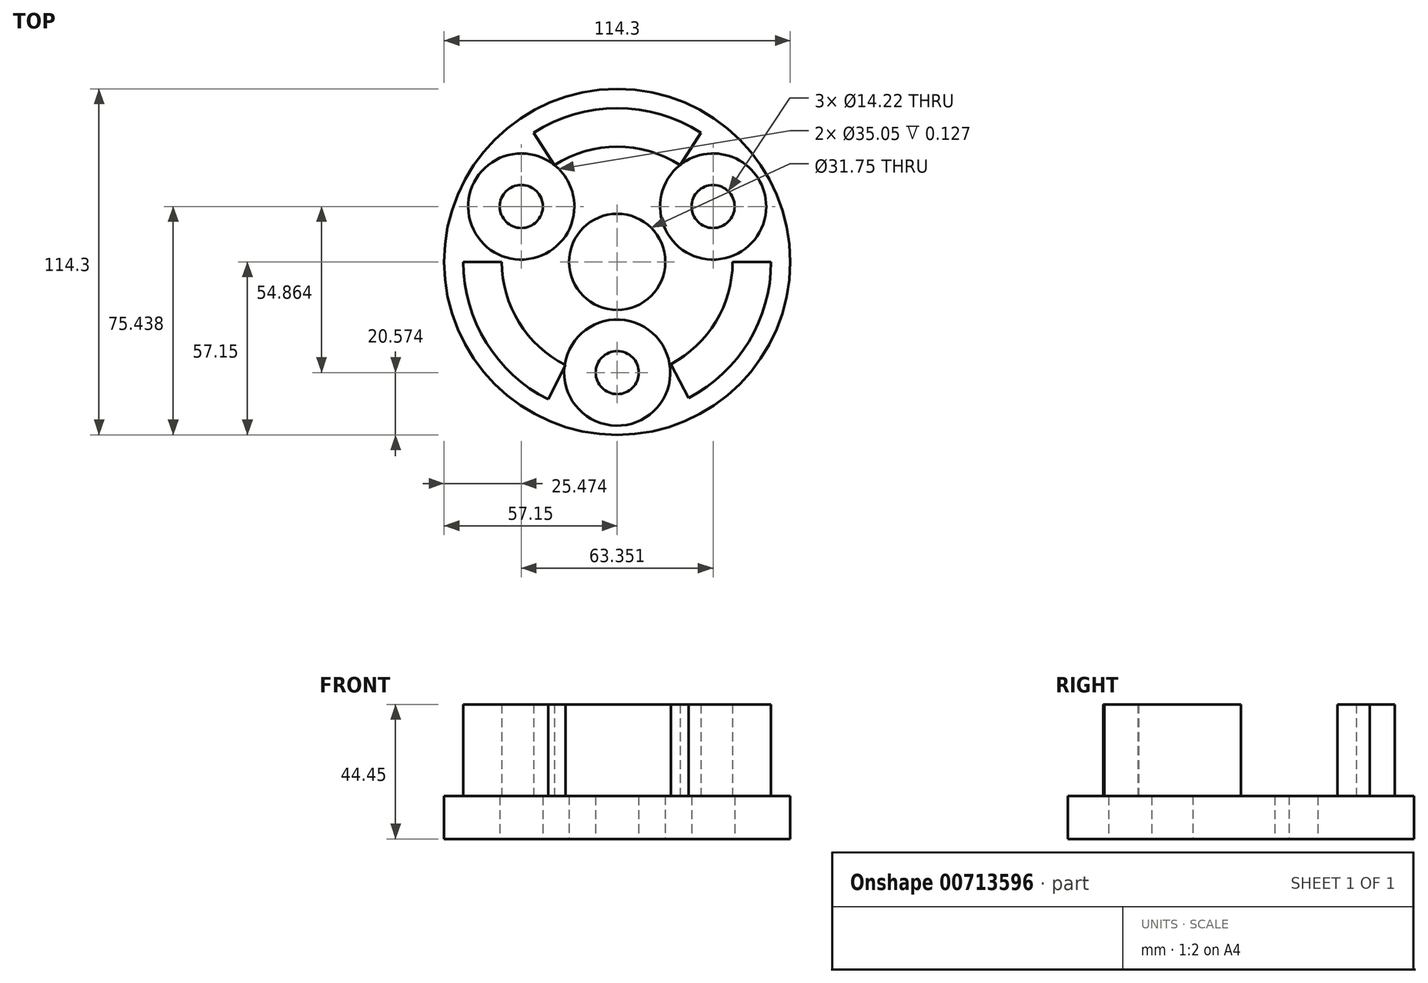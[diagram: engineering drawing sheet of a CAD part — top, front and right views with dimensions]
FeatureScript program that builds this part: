
annotation { "Feature Type Name" : "Feature", "Feature Type Description" : "" }
export const myFeature = defineFeature(function(context is Context, id is Id, definition is map)
    precondition{}
    {
        {
            var Q0;
            Q0=qCreatedBy(makeId("Top.planeOp"),FACE);
            var sketch = newSketch(context, id + "F0", { "sketchPlane" : qUnion([Q0])});
            skCircle(sketch, "E0", {"center": v(0, 0) * mm, "radius": 57.15 * mm});
            skCircle(sketch, "E1", {"center": v(0, 0) * mm, "radius": 36.58 * mm, "construction": true});
            skCircle(sketch, "E2", {"center": v(0, -36.58) * mm, "radius": 7.11 * mm});
            skCircle(sketch, "E3.1.0", {"center": v(31.68, 18.29) * mm, "radius": 7.11 * mm});
            skCircle(sketch, "E3.2.0", {"center": v(-31.68, 18.29) * mm, "radius": 7.11 * mm});
            skLineSegment(sketch, "E4", {"start": v(0, 0) * mm, "end": v(-31.68, 18.29) * mm});
            skLineSegment(sketch, "E5", {"start": v(0, 0) * mm, "end": v(31.68, 18.29) * mm});
            skLineSegment(sketch, "E6", {"start": v(0, 0) * mm, "end": v(0, -36.58) * mm});
            skCircle(sketch, "E7", {"center": v(0, 0) * mm, "radius": 15.88 * mm});
            skSolve(sketch);
        }
        {
            var Q0;
            Q0 = qSketchRegion(id + "F0", true);
            extrude(context, id + "F1", {"entities" : qUnion([Q0]), "depth" : 14.22 * mm, "offsetDistance" : 25.4 * mm});
        }
        {
            var Q0;
            Q0=makeQuery(id+"F1.opExtrude","CAP_FACE",FACE,{"disambiguationData":[OSD([sQuery(id+"F0.wireOp",EDGE,"E0"),sQuery(id+"F0.wireOp",EDGE,"E2"),sQuery(id+"F0.wireOp",EDGE,"E3.1.0"),sQuery(id+"F0.wireOp",EDGE,"E3.2.0")])],"isStart":false});
            var sketch = newSketch(context, id + "F2", { "sketchPlane" : qUnion([Q0])});
            skArc(sketch, "E8", {"start": v(-38.1, 0) * mm, "mid": v(-32.43, -20) * mm, "end": v(-17.12, -34.04) * mm});
            skArc(sketch, "E9.0", {"start": v(-50.8, 0) * mm, "mid": v(-43.24, -26.66) * mm, "end": v(-22.83, -45.38) * mm});
            skArc(sketch, "E10.trimOffspring", {"start": v(20.72, 31.97) * mm, "mid": v(0, 38.1) * mm, "end": v(-20.72, 31.97) * mm});
            skArc(sketch, "E11.trimOffspring", {"start": v(17.69, -33.74) * mm, "mid": v(32.6, -19.72) * mm, "end": v(38.1, 0) * mm});
            skLineSegment(sketch, "E12", {"start": v(-20.72, 31.97) * mm, "end": v(-27.63, 42.63) * mm});
            skLineSegment(sketch, "E13", {"start": v(20.72, 31.97) * mm, "end": v(27.63, 42.63) * mm});
            skArc(sketch, "E14.trimOffspring", {"start": v(27.63, 42.63) * mm, "mid": v(0, 50.8) * mm, "end": v(-27.63, 42.63) * mm});
            skLineSegment(sketch, "E15", {"start": v(-38.1, 0) * mm, "end": v(-50.8, 0) * mm});
            skLineSegment(sketch, "E16", {"start": v(-17.12, -34.04) * mm, "end": v(-22.83, -45.38) * mm});
            skLineSegment(sketch, "E17", {"start": v(17.69, -33.74) * mm, "end": v(23.59, -45) * mm});
            skLineSegment(sketch, "E18", {"start": v(38.1, 0) * mm, "end": v(50.8, 0) * mm});
            skArc(sketch, "E19.trimOffspring", {"start": v(23.59, -45) * mm, "mid": v(43.47, -26.3) * mm, "end": v(50.8, 0) * mm});
            skSolve(sketch);
        }
        {
            var Q0;
            Q0 = qSketchRegion(id + "F2", true);
            extrude(context, id + "F3", {"entities" : qUnion([Q0]), "operationType" : NewBodyOperationType.ADD, "depth" : 30.23 * mm, "offsetDistance" : 25.4 * mm});
        }
        {
            var Q0;
            Q0=makeQuery(id+"F1.opExtrude","CAP_FACE",FACE,{"disambiguationData":[OSD([sQuery(id+"F0.wireOp",EDGE,"E0"),sQuery(id+"F0.wireOp",EDGE,"E2"),sQuery(id+"F0.wireOp",EDGE,"E3.1.0"),sQuery(id+"F0.wireOp",EDGE,"E3.2.0"),sQuery(id+"F0.wireOp",EDGE,"E7")])],"isStart":false});
            var sketch = newSketch(context, id + "F4", { "sketchPlane" : qUnion([Q0])});
            skCircle(sketch, "E20", {"center": v(-31.68, 18.29) * mm, "radius": 17.53 * mm});
            skCircle(sketch, "E21", {"center": v(31.68, 18.29) * mm, "radius": 17.53 * mm});
            skCircle(sketch, "E22", {"center": v(0, -36.58) * mm, "radius": 17.53 * mm});
            skSolve(sketch);
        }
        {
            var Q0;
            Q0=makeQuery(id+"F4.imprint","IMPRINT",FACE,{"disambiguationData":[TD([[makeQuery(id+"F4.imprint","IMPRINT",EDGE,{"derivedFrom":sQuery(id+"F4.wireOp",EDGE,"E20")}),1.0]])]});
            var Q1;
            Q1=makeQuery(id+"F4.imprint","IMPRINT",FACE,{"disambiguationData":[TD([[makeQuery(id+"F4.imprint","IMPRINT",EDGE,{"derivedFrom":sQuery(id+"F4.wireOp",EDGE,"E21")}),1.0]])]});
            var Q2;
            Q2=makeQuery(id+"F4.imprint","IMPRINT",FACE,{"disambiguationData":[TD([[makeQuery(id+"F4.imprint","IMPRINT",EDGE,{"derivedFrom":makeQuery(id+"F1.opExtrude","CAP_EDGE",EDGE,{"disambiguationData":[OSD([sQuery(id+"F0.wireOp",EDGE,"E2")])],"isStart":false})}),-1.0]])]});
            extrude(context, id + "F5", {"entities" : qUnion([Q0, Q1, Q2]), "operationType" : NewBodyOperationType.REMOVE, "oppositeDirection" : true, "depth" : 0.13 * mm, "offsetDistance" : 25.4 * mm});
        }
    });
